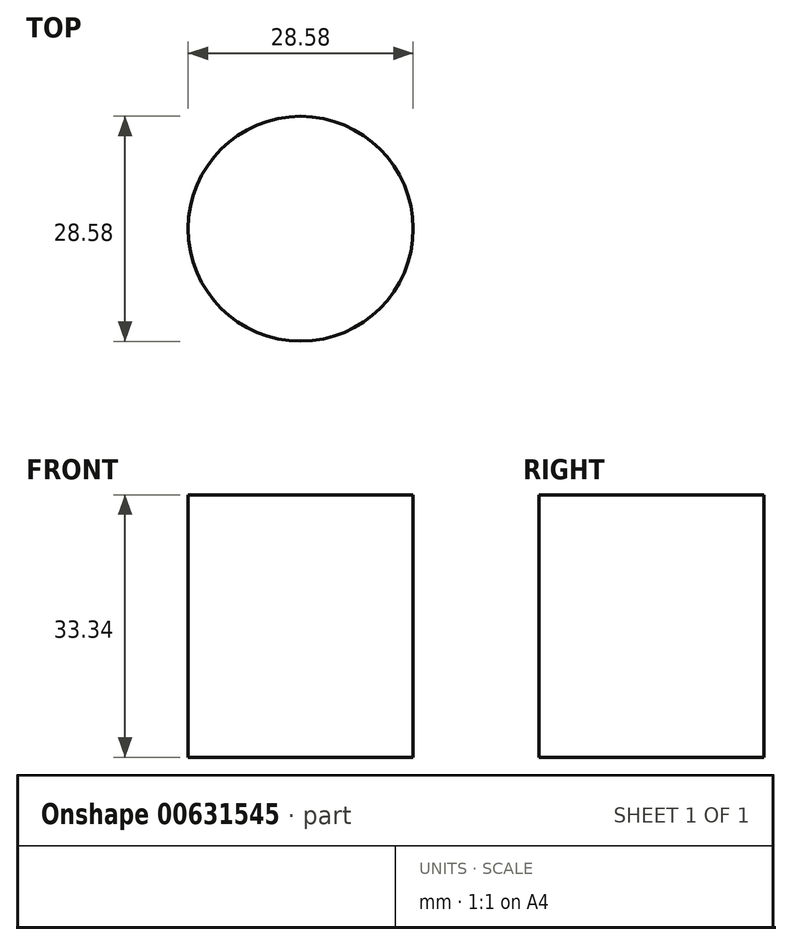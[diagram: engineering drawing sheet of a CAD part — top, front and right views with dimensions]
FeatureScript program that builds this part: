
annotation { "Feature Type Name" : "Feature", "Feature Type Description" : "" }
export const myFeature = defineFeature(function(context is Context, id is Id, definition is map)
    precondition{}
    {
        {
            var Q0;
            Q0=qCreatedBy(makeId("Top.planeOp"),FACE);
            var sketch = newSketch(context, id + "F0", { "sketchPlane" : qUnion([Q0])});
            skCircle(sketch, "E0", {"center": v(0, 0) * mm, "radius": 14.29 * mm});
            skSolve(sketch);
        }
        {
            var Q0;
            Q0 = qSketchRegion(id + "F0", true);
            extrude(context, id + "F1", {"entities" : qUnion([Q0]), "depth" : 33.34 * mm, "offsetDistance" : 25.4 * mm});
        }
    });
